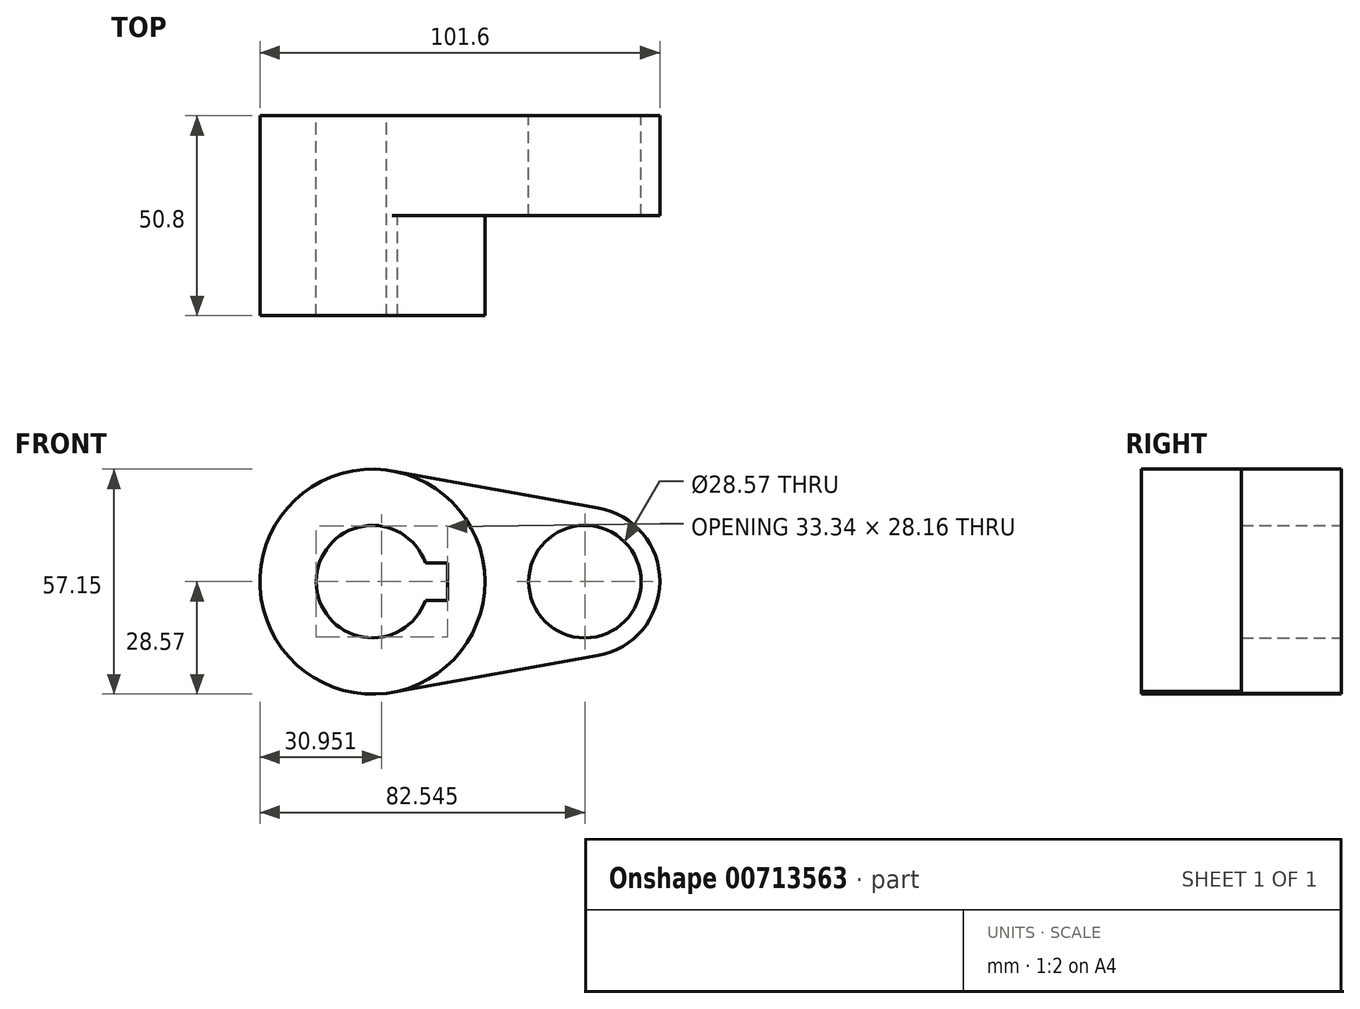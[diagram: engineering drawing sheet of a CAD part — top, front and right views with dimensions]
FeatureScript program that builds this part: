
annotation { "Feature Type Name" : "Feature", "Feature Type Description" : "" }
export const myFeature = defineFeature(function(context is Context, id is Id, definition is map)
    precondition{}
    {
        {
            var Q0;
            Q0=qCreatedBy(makeId("Front.planeOp"),FACE);
            var sketch = newSketch(context, id + "F0", { "sketchPlane" : qUnion([Q0])});
            skCircle(sketch, "E0", {"center": v(0, 0) * mm, "radius": 28.58 * mm});
            skCircle(sketch, "E1", {"center": v(53.98, 0) * mm, "radius": 19.05 * mm});
            skLineSegment(sketch, "E2", {"start": v(5.04, 28.13) * mm, "end": v(57.34, 18.75) * mm});
            skLineSegment(sketch, "E3", {"start": v(3.64, -28.34) * mm, "end": v(57.34, -18.75) * mm});
            skCircle(sketch, "E4", {"center": v(0, 0) * mm, "radius": 14.29 * mm});
            skCircle(sketch, "E5", {"center": v(53.98, 0) * mm, "radius": 14.29 * mm});
            skLineSegment(sketch, "E6.bottom", {"start": v(19.05, -4.76) * mm, "end": v(-19.05, -4.76) * mm});
            skLineSegment(sketch, "E6.top", {"start": v(19.05, 4.76) * mm, "end": v(-19.05, 4.76) * mm});
            skLineSegment(sketch, "E6.left", {"start": v(19.05, -4.76) * mm, "end": v(19.05, 4.76) * mm});
            skLineSegment(sketch, "E6.right", {"start": v(-19.05, -4.76) * mm, "end": v(-19.05, 4.76) * mm});
            skSolve(sketch);
        }
        {
            var Q0;
            {var subQ4=sQuery(id+"F0.wireOp",EDGE,"E6.left");Q0=makeQuery(id+"F0.imprint","IMPRINT",FACE,{"disambiguationData":[TD([[makeQuery(id+"F0.imprint","IMPRINT",EDGE,{"derivedFrom":subQ4}),-1.0]])]});}
            var Q1;
            {var subQ0=sQuery(id+"F0.wireOp",EDGE,"E2");Q1=makeQuery(id+"F0.imprint","IMPRINT",FACE,{"disambiguationData":[TD([[makeQuery(id+"F0.imprint","IMPRINT",EDGE,{"derivedFrom":subQ0}),-1.0]])]});}
            var Q2;
            Q2=makeQuery(id+"F0.imprint","IMPRINT",FACE,{"disambiguationData":[TD([[makeQuery(id+"F0.imprint","IMPRINT",EDGE,{"derivedFrom":sQuery(id+"F0.wireOp",EDGE,"E5")}),-1.0]])]});
            var Q3;
            {var subQ5=sQuery(id+"F0.wireOp",EDGE,"E6.right");Q3=makeQuery(id+"F0.imprint","IMPRINT",FACE,{"disambiguationData":[TD([[makeQuery(id+"F0.imprint","IMPRINT",EDGE,{"derivedFrom":subQ5}),-1.0]])]});}
            extrude(context, id + "F1", {"entities" : qUnion([Q0, Q1, Q2, Q3]), "depth" : 25.4 * mm, "offsetDistance" : 25.4 * mm});
        }
        {
            var Q0;
            {var subQ4=sQuery(id+"F0.wireOp",EDGE,"E6.left");Q0=makeQuery(id+"F0.imprint","IMPRINT",FACE,{"disambiguationData":[TD([[makeQuery(id+"F0.imprint","IMPRINT",EDGE,{"derivedFrom":subQ4}),-1.0]])]});}
            var Q1;
            {var subQ5=sQuery(id+"F0.wireOp",EDGE,"E6.right");Q1=makeQuery(id+"F0.imprint","IMPRINT",FACE,{"disambiguationData":[TD([[makeQuery(id+"F0.imprint","IMPRINT",EDGE,{"derivedFrom":subQ5}),-1.0]])]});}
            extrude(context, id + "F2", {"entities" : qUnion([Q0, Q1]), "operationType" : NewBodyOperationType.ADD, "depth" : 50.8 * mm, "offsetDistance" : 25.4 * mm});
        }
    });
